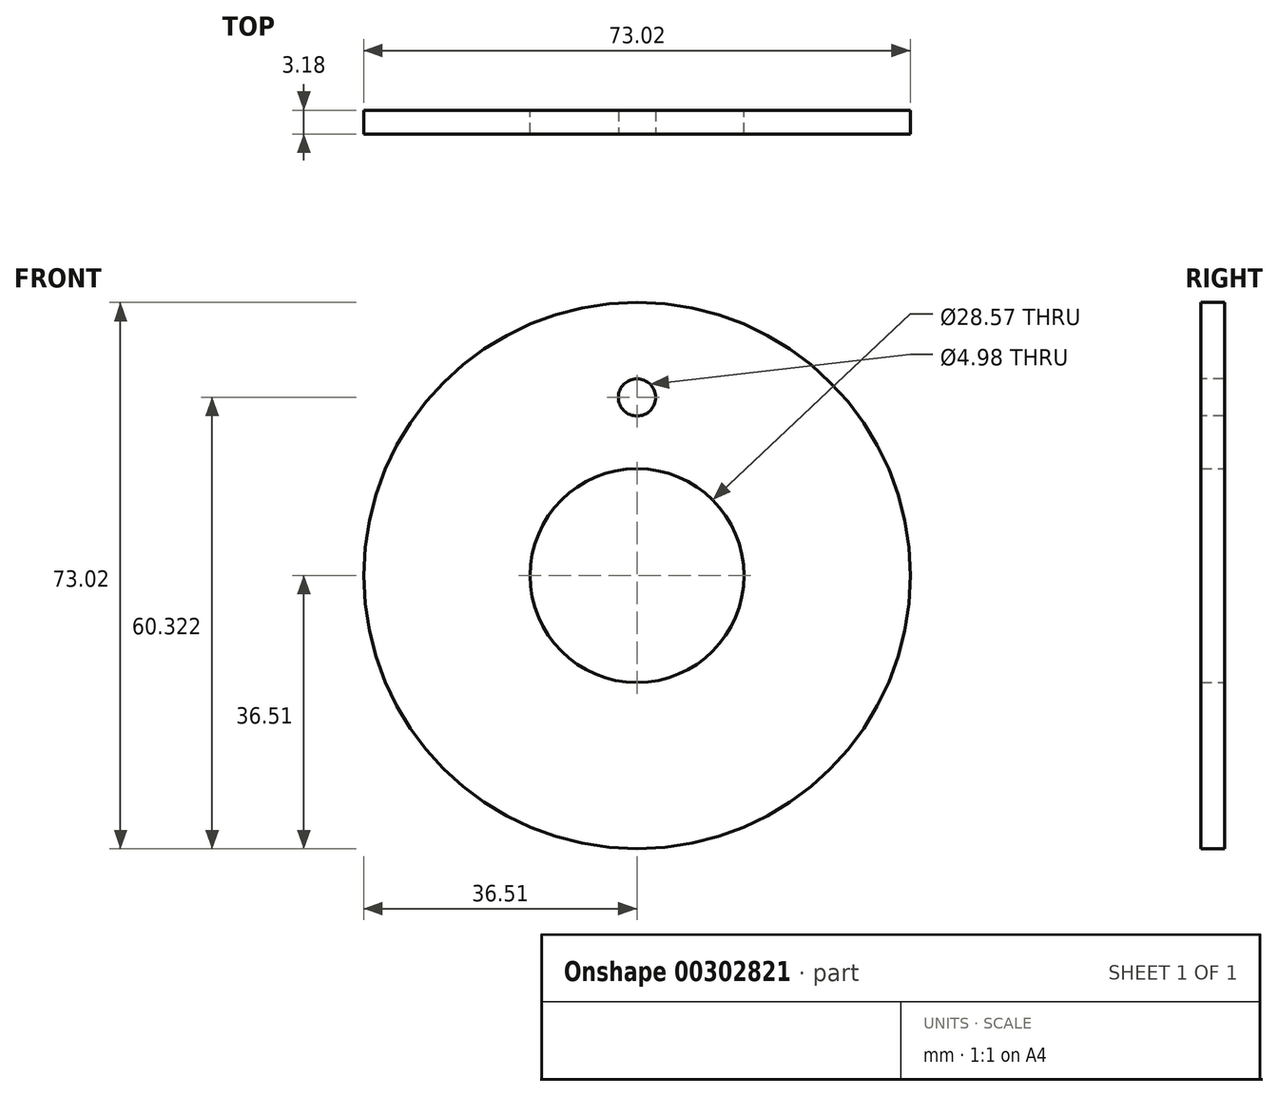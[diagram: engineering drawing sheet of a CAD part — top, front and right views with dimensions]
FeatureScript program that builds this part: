
annotation { "Feature Type Name" : "Feature", "Feature Type Description" : "" }
export const myFeature = defineFeature(function(context is Context, id is Id, definition is map)
    precondition{}
    {
        {
            var Q0;
            Q0=qCreatedBy(makeId("Front.planeOp"),FACE);
            var sketch = newSketch(context, id + "F0", { "sketchPlane" : qUnion([Q0])});
            skCircle(sketch, "E0", {"center": v(0, 0) * mm, "radius": 36.51 * mm});
            skCircle(sketch, "E1", {"center": v(0, 0) * mm, "radius": 14.29 * mm});
            skSolve(sketch);
        }
        {
            var Q0;
            Q0 = qSketchRegion(id + "F0", true);
            extrude(context, id + "F1", {"entities" : qUnion([Q0]), "depth" : 3.17 * mm});
        }
        {
            var Q0;
            Q0=makeQuery(id+"F1.opExtrude","CAP_FACE",FACE,{"disambiguationData":[OSD([sQuery(id+"F0.wireOp",EDGE,"E0"),sQuery(id+"F0.wireOp",EDGE,"E1")])],"isStart":false});
            var sketch = newSketch(context, id + "F2", { "sketchPlane" : qUnion([Q0])});
            skCircle(sketch, "E2", {"center": v(0, 23.81) * mm, "radius": 2.49 * mm});
            skSolve(sketch);
        }
        {
            var Q0;
            Q0 = qSketchRegion(id + "F2", true);
            extrude(context, id + "F3", {"entities" : qUnion([Q0]), "operationType" : NewBodyOperationType.REMOVE, "endBound" : BoundingType.THROUGH_ALL, "oppositeDirection" : true, "depth" : 25.4 * mm});
        }
    });
